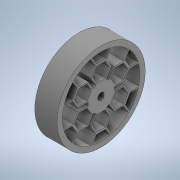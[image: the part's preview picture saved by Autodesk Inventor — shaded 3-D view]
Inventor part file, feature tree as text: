
AUTODESK INVENTOR PART (.ipt)
format: ipt  version: 2020 (Build 240168000, 168)  size: 463,360 bytes
history: native  units: in
note: dims shown in document units (in); Inventor stores cm internally (conversion verified against a paired STEP export)
features: extrude x1
ambient origin geometry x8: Origin, YZ Plane, XZ Plane, XY Plane, X Axis, Y Axis, Z Axis, Center Point
bodies: Solid1 (feature_tree)
feature tree (1):
  extrude  "Extrusion2"  Depth=0.1181in
